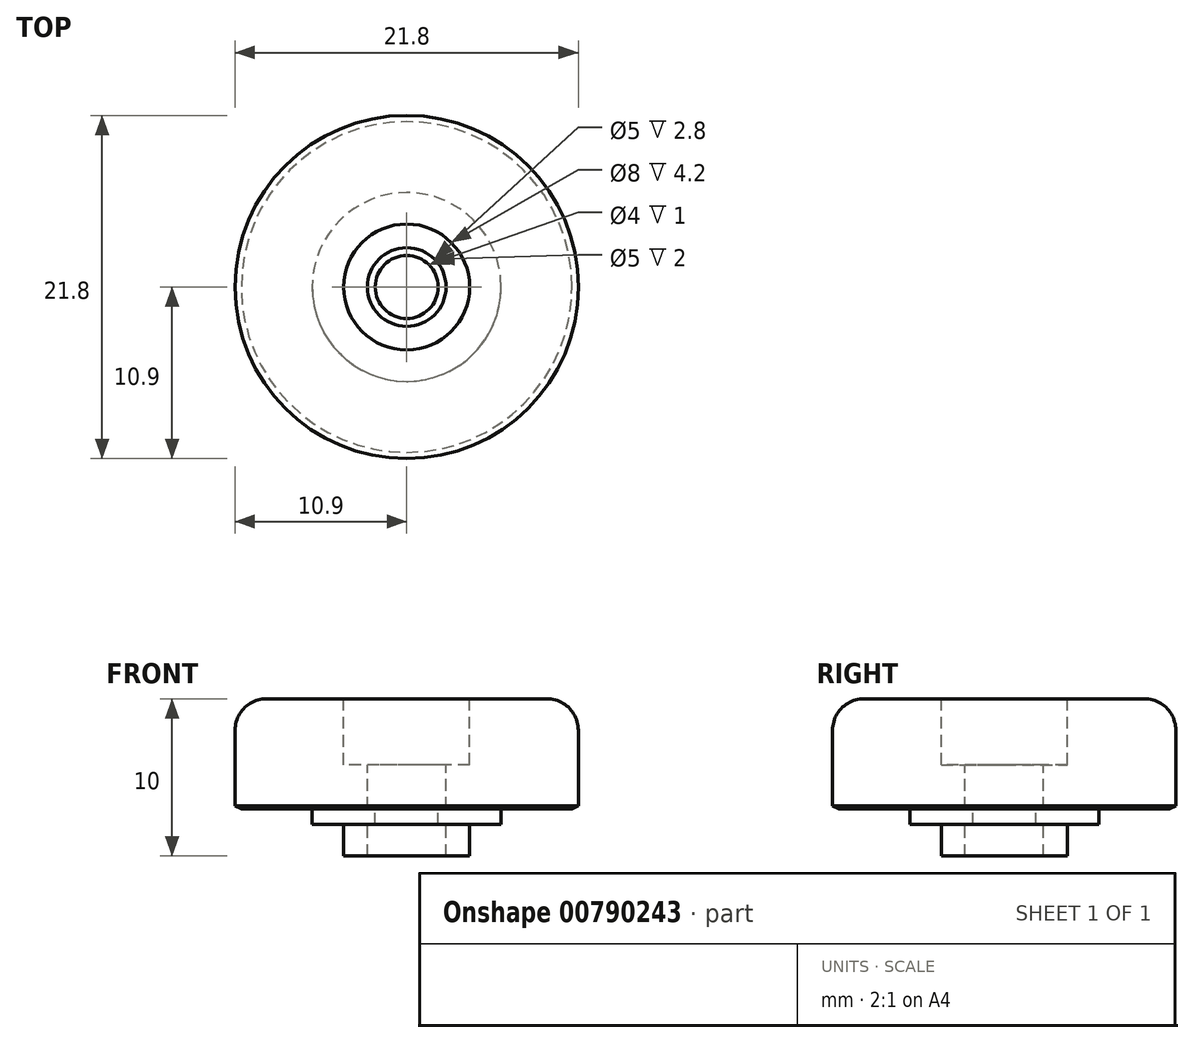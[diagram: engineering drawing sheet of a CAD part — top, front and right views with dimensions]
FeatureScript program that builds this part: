
annotation { "Feature Type Name" : "Feature", "Feature Type Description" : "" }
export const myFeature = defineFeature(function(context is Context, id is Id, definition is map)
    precondition{}
    {
        {
            var Q0;
            Q0=qCreatedBy(makeId("Top.planeOp"),FACE);
            var sketch = newSketch(context, id + "F0", { "sketchPlane" : qUnion([Q0])});
            skCircle(sketch, "E0", {"center": v(0, 0) * mm, "radius": 10.9 * mm});
            skSolve(sketch);
        }
        {
            var Q0;
            Q0 = qSketchRegion(id + "F0", true);
            extrude(context, id + "F1", {"entities" : qUnion([Q0]), "depth" : 7 * mm, "offsetDistance" : 25 * mm});
        }
        {
            var Q0;
            Q0=makeQuery(id+"F1.opExtrude","CAP_EDGE",EDGE,{"disambiguationData":[OSD([sQuery(id+"F0.wireOp",EDGE,"E0")])],"isStart":true});
            chamfer(context, id + "F2", {"entities" : qUnion([Q0]), "chamferType" : ChamferType.TWO_OFFSETS, "width1" : .2 * mm, "oppositeDirection" : false, "width2" : .4 * mm, "tangentPropagation" : true});
        }
        {
            var Q0;
            Q0=makeQuery(id+"F1.opExtrude","CAP_EDGE",EDGE,{"disambiguationData":[OSD([sQuery(id+"F0.wireOp",EDGE,"E0")])],"isStart":false});
            fillet(context, id + "F3", {"entities" : qUnion([Q0]), "radius" : 2 * mm, "tangentPropagation" : true, "allowEdgeOverflow" : false});
        }
        {
            var Q0;
            Q0=makeQuery(id+"F1.opExtrude","CAP_FACE",FACE,{"disambiguationData":[OSD([sQuery(id+"F0.wireOp",EDGE,"E0")])],"isStart":true});
            var sketch = newSketch(context, id + "F4", { "sketchPlane" : qUnion([Q0])});
            skCircle(sketch, "E1", {"center": v(0, 0) * mm, "radius": 4 * mm});
            skSolve(sketch);
        }
        {
            var Q0;
            Q0 = qSketchRegion(id + "F4", true);
            extrude(context, id + "F5", {"entities" : qUnion([Q0]), "operationType" : NewBodyOperationType.ADD, "depth" : 3 * mm, "offsetDistance" : 25 * mm});
        }
        {
            var Q0;
            Q0=makeQuery(id+"F1.opExtrude","CAP_FACE",FACE,{"disambiguationData":[OSD([sQuery(id+"F0.wireOp",EDGE,"E0")])],"isStart":false});
            var sketch = newSketch(context, id + "F6", { "sketchPlane" : qUnion([Q0])});
            skPoint(sketch, "E2", {"position": v(0, 0) * mm});
            skSolve(sketch);
        }
        {
            var Q0;
            Q0=sQuery(id+"F6.wireOp",VERTEX,"E2");
            var Q1;
            Q1=makeQuery(id+"F1.opExtrude","SWEPT_BODY",BODY,{"disambiguationData":[OSD([sQuery(id+"F0.wireOp",EDGE,"E0")])]});
            hole(context, id + "F7", {"style" : HoleStyle.C_BORE, "endStyle" : HoleEndStyle.BLIND, "holeDiameter" : 5 * mm, "cBoreDiameter" : 8 * mm, "cBoreDepth" : 4.2 * mm, "majorDiameter" : 5 * mm, "holeDepth" : 10 * mm, "isTappedThrough" : true, "tappedDepth" : 12 * mm, "tapClearance" : 3, "startFromSketch" : true, "locations" : qUnion([Q0]), "scope" : qUnion([Q1])});
        }
        {
            var Q0;
            Q0=makeQuery(id+"F1.opExtrude","CAP_FACE",FACE,{"disambiguationData":[OSD([sQuery(id+"F0.wireOp",EDGE,"E0")])],"isStart":true});
            var sketch = newSketch(context, id + "F8", { "sketchPlane" : qUnion([Q0])});
            skCircle(sketch, "E3", {"center": v(0, 0) * mm, "radius": 6 * mm});
            skCircle(sketch, "E4", {"center": v(0, 0) * mm, "radius": 2 * mm});
            skSolve(sketch);
        }
        {
            var Q0;
            Q0 = qSketchRegion(id + "F8", true);
            extrude(context, id + "F9", {"entities" : qUnion([Q0]), "operationType" : NewBodyOperationType.ADD, "depth" : 1 * mm, "offsetDistance" : 25 * mm});
        }
    });
